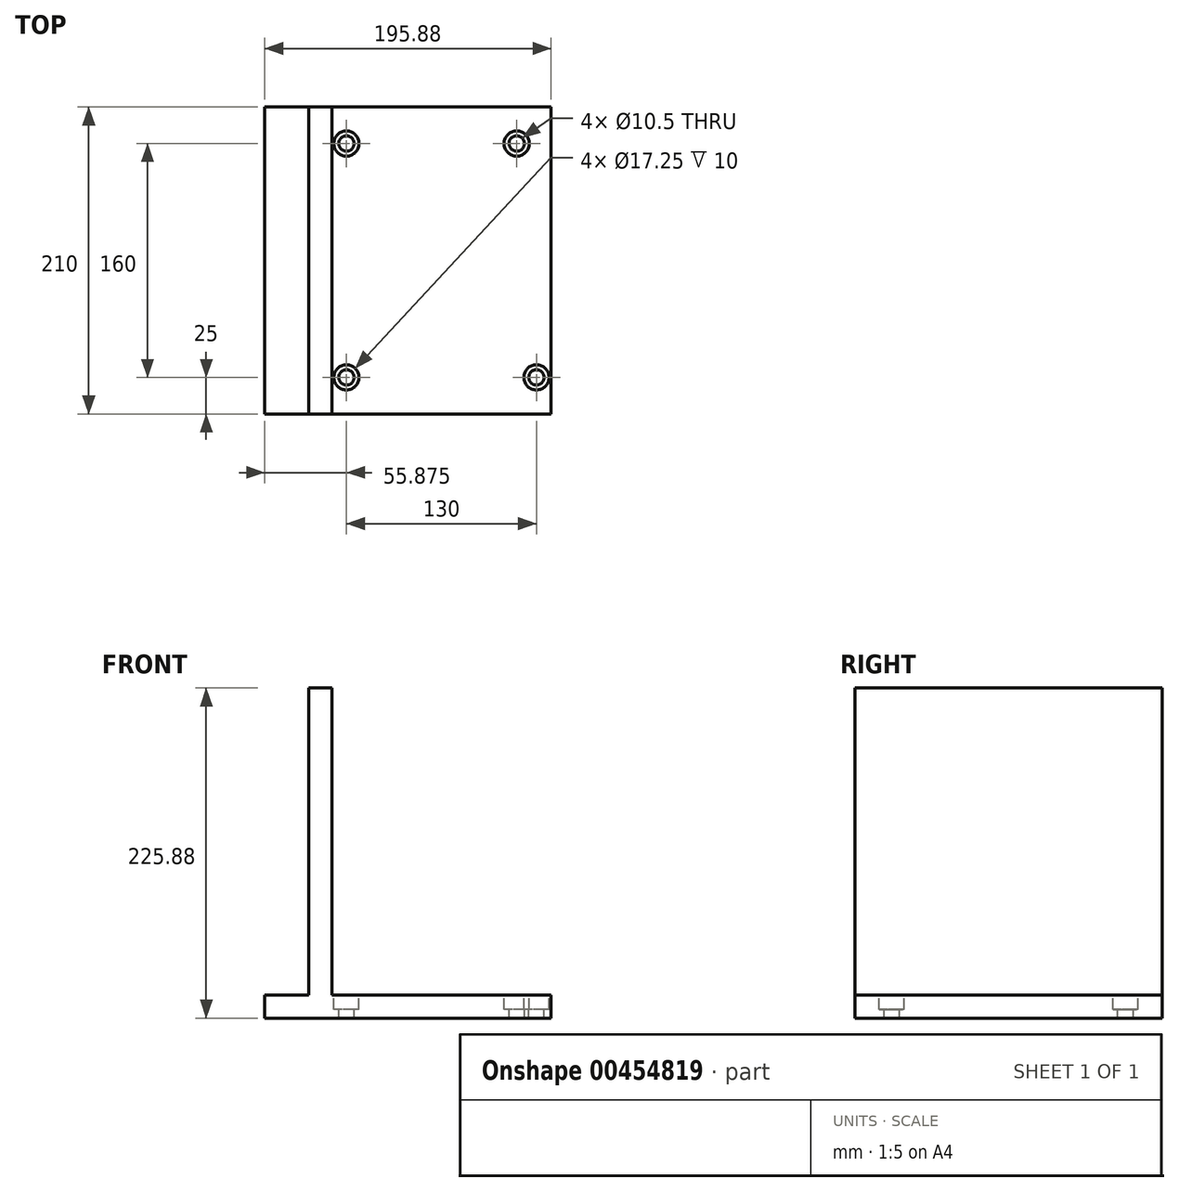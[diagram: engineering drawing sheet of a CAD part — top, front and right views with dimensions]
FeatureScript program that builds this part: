
annotation { "Feature Type Name" : "Feature", "Feature Type Description" : "" }
export const myFeature = defineFeature(function(context is Context, id is Id, definition is map)
    precondition{}
    {
        {
            var Q0;
            Q0=qCreatedBy(makeId("Front.planeOp"),FACE);
            var sketch = newSketch(context, id + "F0", { "sketchPlane" : qUnion([Q0])});
            skLineSegment(sketch, "E0", {"start": v(0, 0) * mm, "end": v(0, 210) * mm});
            skLineSegment(sketch, "E1", {"start": v(0, 210) * mm, "end": v(15.87, 210) * mm});
            skLineSegment(sketch, "E2", {"start": v(15.88, 210) * mm, "end": v(15.88, 0) * mm});
            skLineSegment(sketch, "E3", {"start": v(15.88, 0) * mm, "end": v(165.88, 0) * mm});
            skLineSegment(sketch, "E4", {"start": v(165.88, 0) * mm, "end": v(165.88, -15.87) * mm});
            skLineSegment(sketch, "E5", {"start": v(165.88, -15.87) * mm, "end": v(-30, -15.88) * mm});
            skLineSegment(sketch, "E6", {"start": v(-30, -15.88) * mm, "end": v(-30, 0) * mm});
            skLineSegment(sketch, "E7", {"start": v(-30, 0) * mm, "end": v(0, 0) * mm});
            skSolve(sketch);
        }
        {
            var Q0;
            Q0=makeQuery(id+"F0.imprint","IMPRINT",FACE,{"disambiguationData":[TD([[makeQuery(id+"F0.imprint","IMPRINT",EDGE,{"derivedFrom":sQuery(id+"F0.wireOp",EDGE,"E0")}),-1.0]])]});
            extrude(context, id + "F1", {"entities" : qUnion([Q0]), "oppositeDirection" : true, "depth" : 210 * mm});
        }
        {
            var Q0;
            Q0=makeQuery(id+"F1.opExtrude","SWEPT_FACE",FACE,{"disambiguationData":[OSD([sQuery(id+"F0.wireOp",EDGE,"E3")])]});
            var sketch = newSketch(context, id + "F2", { "sketchPlane" : qUnion([Q0])});
            skPoint(sketch, "E8", {"position": v(142.36, 185) * mm});
            skPoint(sketch, "E9", {"position": v(25.87, 185) * mm});
            skPoint(sketch, "E10", {"position": v(25.87, 25) * mm});
            skPoint(sketch, "E11", {"position": v(155.88, 25) * mm});
            skSolve(sketch);
        }
        {
            var Q0;
            Q0=sQuery(id+"F2.wireOp",VERTEX,"E10");
            var Q1;
            Q1=sQuery(id+"F2.wireOp",VERTEX,"E11");
            var Q2;
            Q2=sQuery(id+"F2.wireOp",VERTEX,"E8");
            var Q3;
            Q3=sQuery(id+"F2.wireOp",VERTEX,"E9");
            var Q4;
            Q4=makeQuery(id+"F1.opExtrude","SWEPT_BODY",BODY,{"disambiguationData":[OSD([sQuery(id+"F0.wireOp",EDGE,"E0"),sQuery(id+"F0.wireOp",EDGE,"E1"),sQuery(id+"F0.wireOp",EDGE,"E2"),sQuery(id+"F0.wireOp",EDGE,"E3"),sQuery(id+"F0.wireOp",EDGE,"E4"),sQuery(id+"F0.wireOp",EDGE,"E5"),sQuery(id+"F0.wireOp",EDGE,"E6"),sQuery(id+"F0.wireOp",EDGE,"E7")])]});
            hole(context, id + "F3", {"style" : HoleStyle.C_BORE, "endStyle" : HoleEndStyle.THROUGH, "standardTappedOrClearance" : lookupTablePath({ "standard" : "ISO", "fit" : "Close", "size" : "M10", "type" : "Clearance" }), "standardBlindInLast" : lookupTablePath({ "fit" : "Close", "standard" : "ISO", "size" : "M10", "type" : "Clearance" }), "holeDiameter" : 10.5 * mm, "cBoreDiameter" : 17.25 * mm, "cBoreDepth" : 10 * mm, "isTappedThrough" : true, "tappedDepth" : 12 * mm, "tapClearance" : 3, "locations" : qUnion([Q0, Q1, Q2, Q3]), "scope" : qUnion([Q4])});
        }
    });
